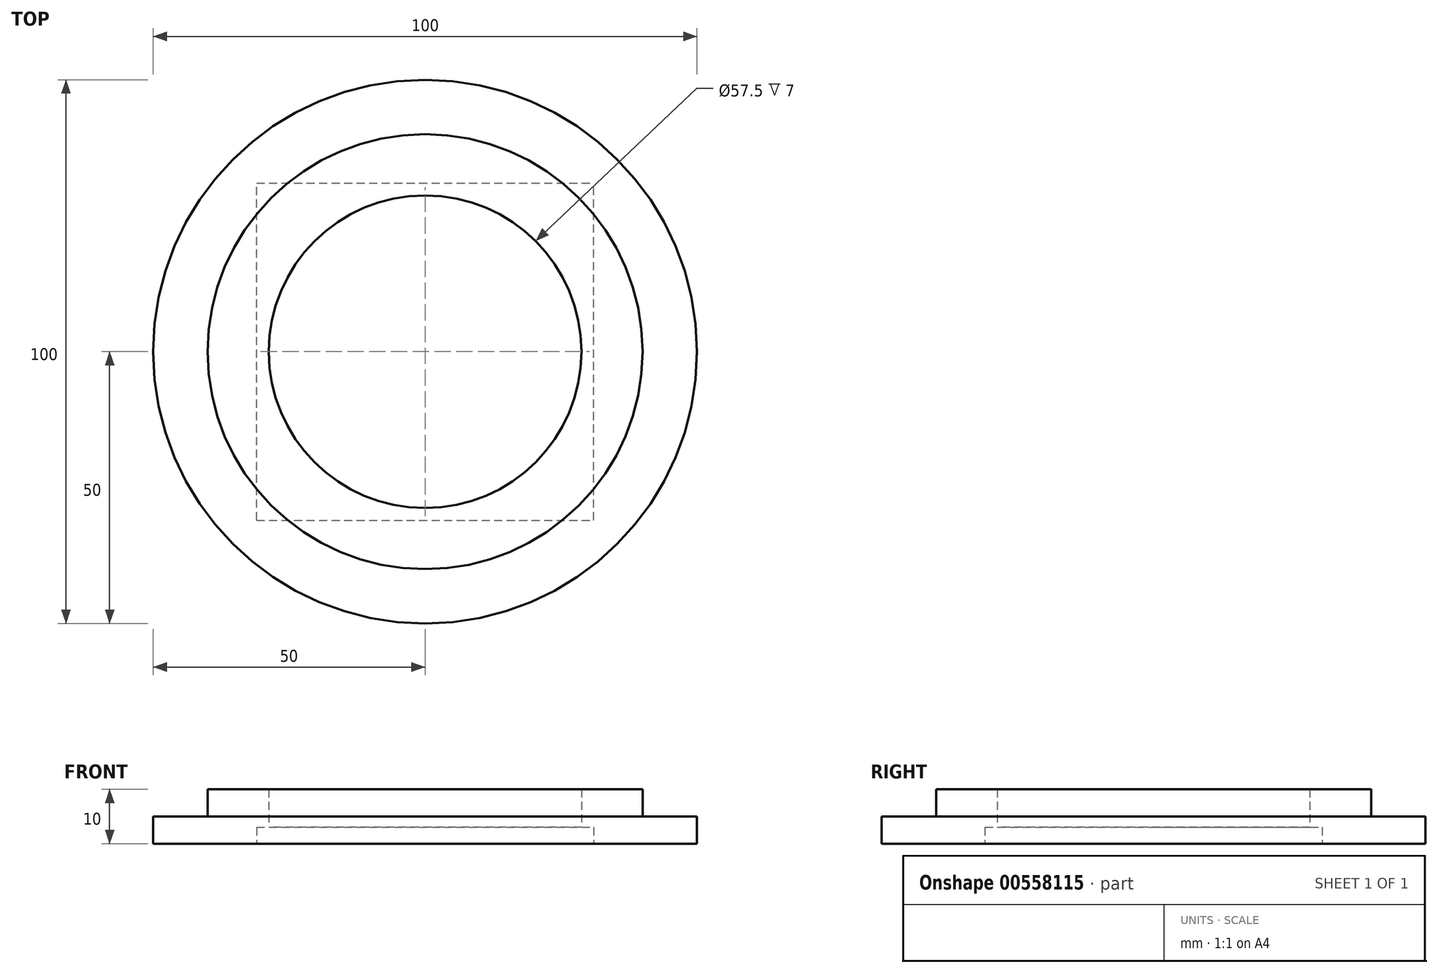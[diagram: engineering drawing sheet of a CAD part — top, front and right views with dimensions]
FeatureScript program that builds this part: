
annotation { "Feature Type Name" : "Feature", "Feature Type Description" : "" }
export const myFeature = defineFeature(function(context is Context, id is Id, definition is map)
    precondition{}
    {
        {
            var Q0;
            Q0=qCreatedBy(makeId("Top.planeOp"),FACE);
            var sketch = newSketch(context, id + "F0", { "sketchPlane" : qUnion([Q0])});
            skCircle(sketch, "E0", {"center": v(0, 0) * mm, "radius": 28.75 * mm});
            skCircle(sketch, "E1", {"center": v(0, 0) * mm, "radius": 40 * mm});
            skCircle(sketch, "E2", {"center": v(0, 0) * mm, "radius": 50 * mm});
            skSolve(sketch);
        }
        {
            var Q0;
            Q0 = qSketchRegion(id + "F0", true);
            var Q1;
            Q1=makeQuery(id+"F0.imprint","IMPRINT",FACE,{"disambiguationData":[TD([[makeQuery(id+"F0.imprint","IMPRINT",EDGE,{"derivedFrom":sQuery(id+"F0.wireOp",EDGE,"E0")}),-1.0]])]});
            extrude(context, id + "F1", {"entities" : qUnion([Q0, Q1]), "depth" : 5 * mm, "offsetDistance" : 25 * mm});
        }
        {
            var Q0;
            Q0=makeQuery(id+"F0.imprint","IMPRINT",FACE,{"disambiguationData":[TD([[makeQuery(id+"F0.imprint","IMPRINT",EDGE,{"derivedFrom":sQuery(id+"F0.wireOp",EDGE,"E0")}),-1.0]])]});
            extrude(context, id + "F2", {"entities" : qUnion([Q0]), "operationType" : NewBodyOperationType.ADD, "depth" : 10 * mm, "offsetDistance" : 25 * mm});
        }
        {
            var Q0;
            Q0=makeQuery(id+"F1.opExtrude","CAP_FACE",FACE,{"disambiguationData":[OSD([sQuery(id+"F0.wireOp",EDGE,"E0"),sQuery(id+"F0.wireOp",EDGE,"E2")])],"isStart":true});
            var sketch = newSketch(context, id + "F3", { "sketchPlane" : qUnion([Q0])});
            skLineSegment(sketch, "E3.bottom", {"start": v(-31, 31) * mm, "end": v(31, 31) * mm});
            skLineSegment(sketch, "E3.top", {"start": v(-31, -31) * mm, "end": v(31, -31) * mm});
            skLineSegment(sketch, "E3.left", {"start": v(-31, 31) * mm, "end": v(-31, -31) * mm});
            skLineSegment(sketch, "E3.right", {"start": v(31, 31) * mm, "end": v(31, -31) * mm});
            skPoint(sketch, "E4", {"position": v(0, 31) * mm});
            skPoint(sketch, "E5", {"position": v(31, 0) * mm});
            skSolve(sketch);
        }
        {
            var Q0;
            Q0=makeQuery(id+"F3.imprint","IMPRINT",FACE,{"disambiguationData":[TD([[makeQuery(id+"F3.imprint","IMPRINT",EDGE,{"derivedFrom":sQuery(id+"F3.wireOp",EDGE,"E3.bottom")}),-1.0]])]});
            extrude(context, id + "F4", {"entities" : qUnion([Q0]), "operationType" : NewBodyOperationType.REMOVE, "oppositeDirection" : true, "depth" : 3 * mm, "offsetDistance" : 25 * mm});
        }
    });
